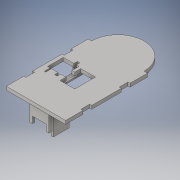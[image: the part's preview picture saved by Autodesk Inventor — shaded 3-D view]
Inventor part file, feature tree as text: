
AUTODESK INVENTOR PART (.ipt)
format: ipt  version: 2016 (Build 200138000, 138)  size: 529,408 bytes
history: native  units: in
note: dims shown in document units (in); Inventor stores cm internally (conversion verified against a paired STEP export)
features: reference x54, extrude x26, sketch x25, plane x6, projected_geometry x2
ambient origin geometry x8: Origin, YZ Plane, XZ Plane, XY Plane, X Axis, Y Axis, Z Axis, Center Point
bodies: Solid1 (feature_tree)
feature tree (113):
  extrude  "Extrusion1"  Depth=3.0in
  extrude  "Extrusion2"  Depth=0.0787in
  extrude  "Extrusion3"  Depth=1.0in
  extrude  "Extrusion4"  Depth=1.0in TaperAngle=0.0deg
  extrude  "Extrusion5"  Depth=0.0197in
  plane  "Work Plane1"
  extrude  "Extrusion6"  Depth=0.0197in
  extrude  "Extrusion7"  Depth=0.0197in
  extrude  "Extrusion8"  Depth=0.0787in
  extrude  "Extrusion9"  Depth=0.303in TaperAngle=0.0deg
  extrude  "Extrusion14"  Depth=0.1575in
  extrude  "Extrusion15"  Depth=0.0787in
  plane  "Work Plane2"
  extrude  "Extrusion16"  Depth=0.1181in TaperAngle=0.0deg
  extrude  "Extrusion17"  Depth=0.1575in
  extrude  "Extrusion18"  Depth=0.1181in TaperAngle=0.0deg
  extrude  "Extrusion19"  Depth=0.0197in
  plane  "Work Plane3"
  extrude  "Extrusion20"  Depth=0.0197in
  extrude  "Extrusion21"  Depth=0.0787in
  plane  "Work Plane4"
  extrude  "Extrusion22"  Depth=1.5748in TaperAngle=0.0deg
  plane  "Work Plane5"
  extrude  "Extrusion23"  Depth=0.9201in TaperAngle=0.0deg
  extrude  "Extrusion24"  Depth=0.1969in
  plane  "Work Plane6"
  extrude  "Extrusion25"  Depth=0.1969in TaperAngle=0.0deg
  extrude  "Extrusion26"  Depth=0.1181in TaperAngle=0.0deg
  extrude  "Extrusion27"  Depth=0.1181in
  extrude  "Extrusion28"  Depth=0.1969in TaperAngle=0.0deg
  extrude  "Extrusion29"  Depth=0.0394in
  extrude  "Extrusion30"  Depth=0.35in
  sketch  "Sketch1"  dims[d0=4.5in d1=3.0in]
  sketch  "Sketch2"  dims[d2=0.1969in d3=0.0in d5=0.0787in]
  reference  "Reference1"
  reference  "Reference2"
  sketch  "Sketch3"  dims[d6=1.0in d7=0.0in d8=1.0827in]
  sketch  "Sketch4"  dims[d9=0.3937in d10=1.0in d11=0.0in]
  reference  "Reference3"
  reference  "Reference4"
  reference  "Reference5"
  reference  "Reference6"
  reference  "Reference7"
  reference  "Reference8"
  reference  "Reference9"
  reference  "Reference10"
  reference  "Reference11"
  reference  "Reference12"
  reference  "Reference13"
  sketch  "Sketch5"  dims[d12=0.0787in d13=0.0197in]
  reference  "Reference14"
  reference  "Reference15"
  reference  "Reference16"
  reference  "Reference17"
  reference  "Reference18"
  sketch  "Sketch6"  dims[d14=0.0197in d15=0.0197in]
  reference  "Reference19"
  sketch  "Sketch7"  dims[d16=0.0197in d17=0.0197in]
  reference  "Reference20"
  reference  "Reference21"
  reference  "Reference22"
  reference  "Reference23"
  reference  "Reference24"
  sketch  "Sketch8"  dims[d18=0.0787in d19=0.0787in]
  reference  "Reference25"
  sketch  "Sketch9"  dims[d20=0.0787in d21=0.303in d22=0.0in]
  projected_geometry  "Projected Loop1"
  projected_geometry  "Projected Loop2"
  sketch  "Sketch14"  dims[d23=0.0098in d24=0.1575in]
  sketch  "Sketch15"  dims[d25=0.0787in d26=0.0098in]
  sketch  "Sketch16"  dims[d27=0.1575in d28=0.1181in d29=0.0in]
  reference  "Reference30"
  sketch  "Sketch17"  dims[d30=1.25in d31=0.1575in]
  reference  "Reference31"
  reference  "Reference32"
  reference  "Reference33"
  reference  "Reference35"
  reference  "Reference36"
  reference  "Reference37"
  reference  "Reference38"
  reference  "Reference39"
  reference  "Reference40"
  reference  "Reference41"
  reference  "Reference42"
  reference  "Reference43"
  reference  "Reference44"
  reference  "Reference45"
  reference  "Reference46"
  reference  "Reference47"
  reference  "Reference48"
  reference  "Reference49"
  sketch  "Sketch19"  dims[d32=0.1575in d33=0.1181in d34=0.0in]
  sketch  "Sketch20"  dims[d35=0.0197in d36=0.0197in]
  reference  "Reference50"
  sketch  "Sketch21"  dims[d37=0.0197in d38=0.0197in]
  sketch  "Sketch22"  dims[d39=0.0787in d40=0.0787in]
  reference  "Reference51"
  reference  "Reference52"
  sketch  "Sketch23"  dims[d41=0.0787in d42=1.5748in d43=0.0in]
  reference  "Reference53"
  reference  "Reference54"
  sketch  "Sketch24"  dims[d44=0.1801in d45=0.0in d46=0.9201in d47=0.0in]
  sketch  "Sketch25"  dims[d58=0.1969in d59=0.1969in]
  reference  "Reference55"
  reference  "Reference56"
  sketch  "Sketch26"  dims[d60=0.1969in d61=0.1969in d62=0.0in]
  reference  "Reference57"
  reference  "Reference58"
  sketch  "Sketch28"  dims[d63=1.0in d64=0.0in d65=0.1181in d66=0.0in]
  sketch  "Sketch29"  dims[d67=0.1969in d68=0.0in d69=0.1181in]
  sketch  "Sketch30"  dims[d70=0.1181in d71=0.1969in d72=0.0in]
  reference  "Reference59"
  sketch  "Sketch31"  dims[d73=0.0787in d74=0.0in d75=0.0394in d76=0.35in d77=0.1628in d78=0.2in d79=0.0787in d80=0.0in d81=0.1969in d82=0.0in d83=0.0098in d84=0.0787in d85=0.0098in d86=0.0787in d87=0.315in d88=0.0in d89=1.5in d90=1.5in d91=0.1181in d92=0.0in d93=0.7in d94=1.26in d95=0.0in d96=0.1181in d97=0.0in d98=0.1181in d99=0.0in d104=1.0in d105=0.1181in d106=0.5in d107=1.0in d108=0.5in d109=10.0in d110=0.0in d111=0.0197in d112=0.0197in d113=0.325in d114=0.197in d115=0.0in d116=0.1969in d117=0.1969in d118=0.1181in d119=0.1969in d120=0.0in d121=0.1575in d122=0.0in]
